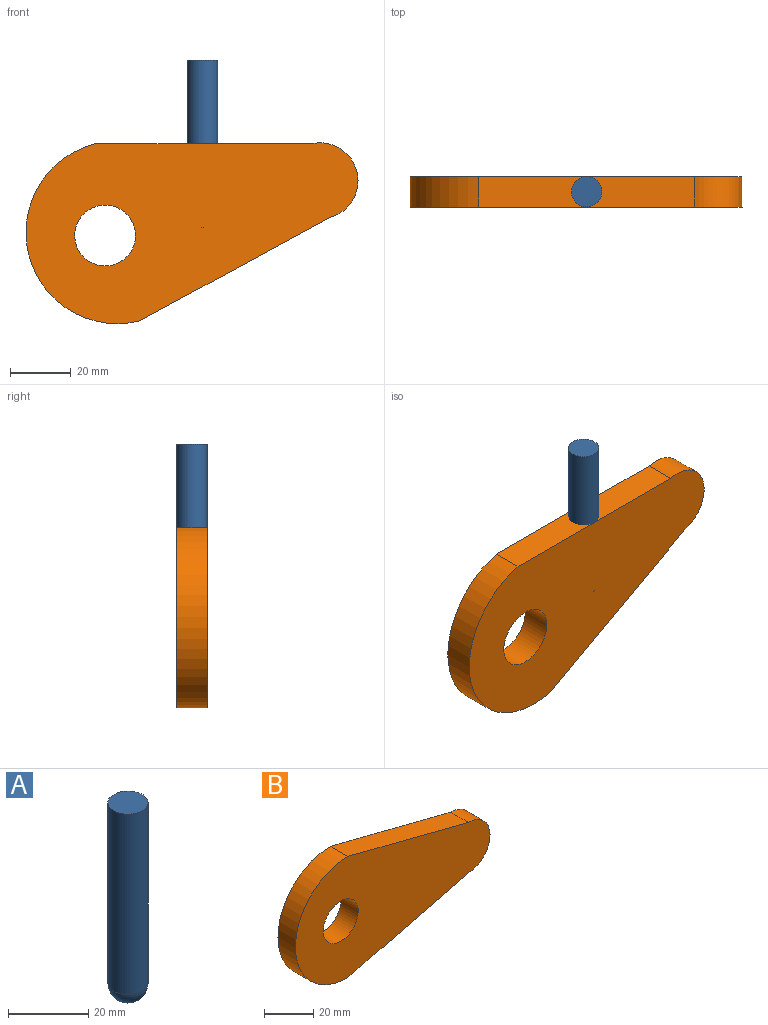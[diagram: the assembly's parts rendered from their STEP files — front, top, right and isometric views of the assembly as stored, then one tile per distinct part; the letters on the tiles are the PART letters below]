
ASSEMBLY  parts=2 mates=1
PART A: 3 faces, bbox 10x10x60 mm
  f0: plane 10x10mm, normal (0,0,1), area 78.5mm2, adj f1
  f1: cylinder r=5mm len=55mm, axis (0,0,-1), area 1727.9mm2, adj f0,f2
  f2: sphere r=5mm, area 157.1mm2, adj f1
PART B: 7 faces, bbox 111.2x10x60 mm
  f0: plane 68.73x17.5mm, normal (0.25,0,0.97), area 709.2mm2, adj f1,f3,f4,f5
  f1: cylinder r=30mm len=60mm, axis (0,1,0), area 942.5mm2, adj f0,f2,f4,f5
  f2: plane 68.73x17.5mm, normal (0.25,0,-0.97), area 709.2mm2, adj f1,f3,f4,f5
  f3: cylinder r=12.5mm len=25mm, axis (0,1,0), area 392.7mm2, adj f0,f2,f4,f5
  f4: plane 111.23x60mm, normal (0,-1,0), area 4266.1mm2, adj f0,f1,f2,f3,f6
  f5: plane 111.23x60mm, normal (0,1,0), area 4266.1mm2, adj f0,f1,f2,f3,f6
  f6: cylinder r=10mm len=20mm, axis (0,-1,0), area 628.3mm2, adj f4,f5
PLACE A rot(axis=(-0.13,0.13,0.98),0deg) t=(-72.86,-55.83,-15.85)mm
PLACE B rot(axis=(0,-1,0),14.3deg) t=(-68.55,-50.83,-4.18)mm
MATE revolute B.f0 <-> A.f1  axis (0,0,1) through (-72.86,-55.83,16.65)mm
